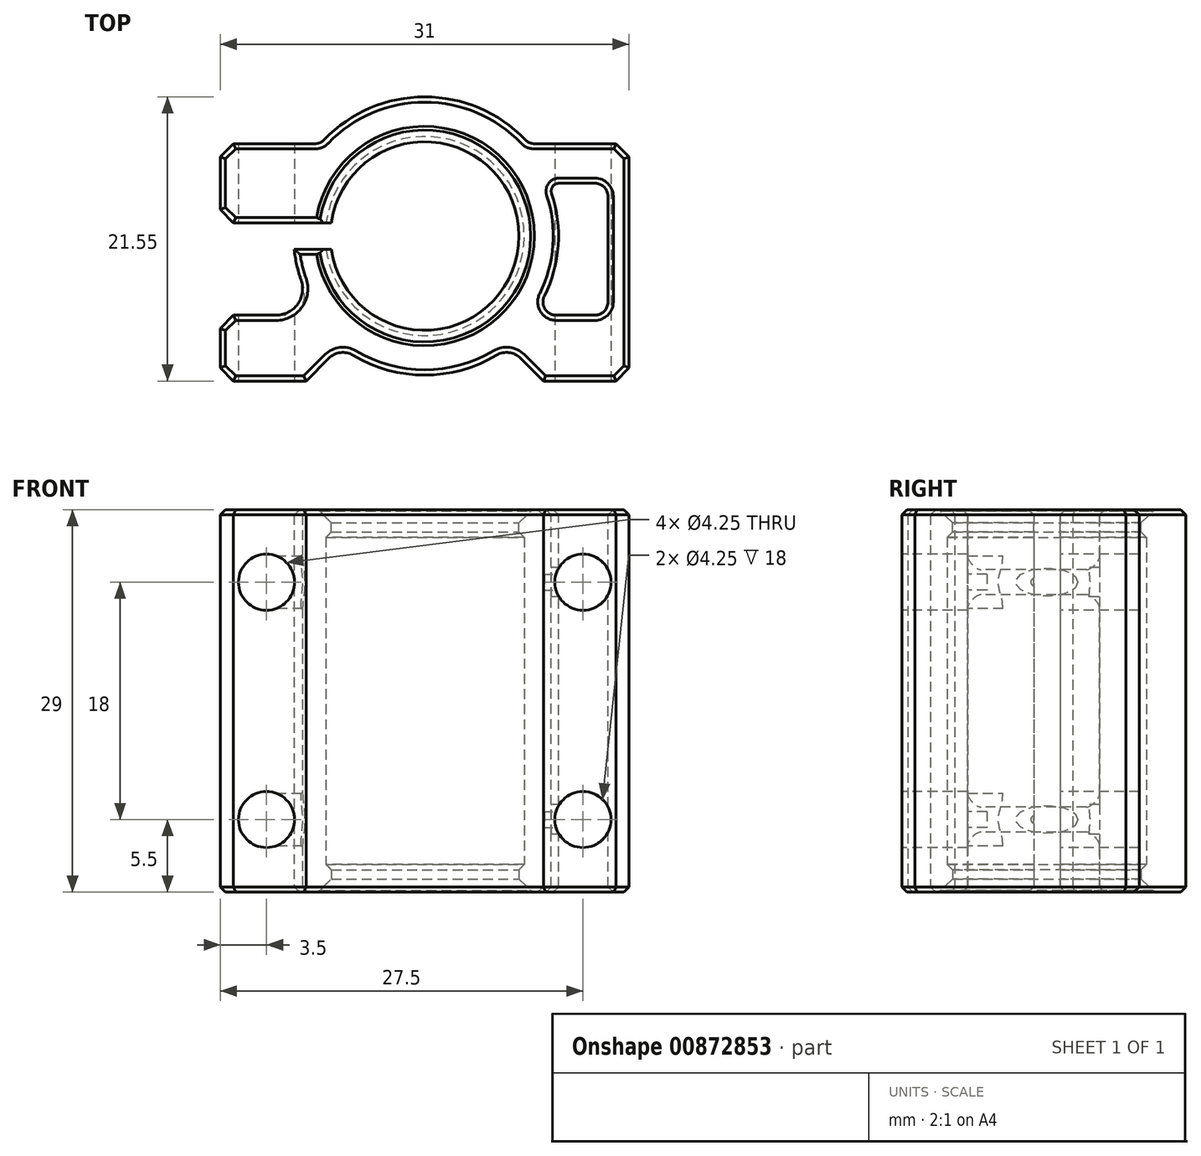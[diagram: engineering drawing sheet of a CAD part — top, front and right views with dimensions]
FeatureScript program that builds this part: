
annotation { "Feature Type Name" : "Feature", "Feature Type Description" : "" }
export const myFeature = defineFeature(function(context is Context, id is Id, definition is map)
    precondition{}
    {
        {
            var Q0;
            Q0=qCreatedBy(makeId("Top.planeOp"),FACE);
            var sketch = newSketch(context, id + "F0", { "sketchPlane" : qUnion([Q0])});
            skLineSegment(sketch, "E0", {"start": v(-15.5, 0) * mm, "end": v(-9, 0) * mm});
            skLineSegment(sketch, "E1", {"start": v(-9, 0) * mm, "end": v(-6.4, 2.6) * mm});
            skLineSegment(sketch, "E2", {"start": v(-15.5, 0) * mm, "end": v(-15.5, 5) * mm});
            skArc(sketch, "E3", {"start": v(0, 18.55) * mm, "mid": v(-4.97, 16.68) * mm, "end": v(-7.48, 12) * mm});
            skArc(sketch, "E4", {"start": v(0, 21.55) * mm, "mid": v(-4.33, 20.62) * mm, "end": v(-7.9, 18) * mm});
            skLineSegment(sketch, "E5", {"start": v(0, -24.75) * mm, "end": v(0, 26.18) * mm, "construction": true});
            skArc(sketch, "E6.MirrorCS", {"start": v(0, 18.55) * mm, "mid": v(7.55, 11) * mm, "end": v(0, 3.45) * mm});
            skArc(sketch, "E7.MirrorCS", {"start": v(0, 21.55) * mm, "mid": v(4.33, 20.62) * mm, "end": v(7.9, 18) * mm});
            skLineSegment(sketch, "E8.MirrorCS", {"start": v(15.5, 0) * mm, "end": v(15.5, 8) * mm});
            skLineSegment(sketch, "E9.MirrorCS", {"start": v(15.5, 0) * mm, "end": v(9, 0) * mm});
            skLineSegment(sketch, "E10.MirrorCS", {"start": v(9, 0) * mm, "end": v(6.4, 2.6) * mm});
            skLineSegment(sketch, "E11", {"start": v(-7.9, 18) * mm, "end": v(-15.5, 18) * mm});
            skLineSegment(sketch, "E12", {"start": v(-15.5, 18) * mm, "end": v(-15.5, 12) * mm});
            skLineSegment(sketch, "E13", {"start": v(-15.5, 12) * mm, "end": v(-10.5, 12) * mm});
            skLineSegment(sketch, "E14", {"start": v(-15.5, 12) * mm, "end": v(-15.5, 10) * mm, "construction": true});
            skLineSegment(sketch, "E15", {"start": v(-10.5, 12) * mm, "end": v(-7.48, 12) * mm});
            skLineSegment(sketch, "E16", {"start": v(-7.48, 10) * mm, "end": v(-9.9, 10) * mm});
            skArc(sketch, "E17.trimOffspring", {"start": v(-7.48, 10) * mm, "mid": v(-4.97, 5.32) * mm, "end": v(0, 3.45) * mm});
            skPoint(sketch, "E18.end.orphan", {"position": v(-8.84, 5.25) * mm});
            skLineSegment(sketch, "E19", {"start": v(7.9, 18) * mm, "end": v(15.5, 18) * mm});
            skLineSegment(sketch, "E20", {"start": v(15.5, 18) * mm, "end": v(15.5, 8) * mm});
            skPoint(sketch, "E21.orphan", {"position": v(8.84, 5.25) * mm});
            skArc(sketch, "E22", {"start": v(-6.4, 2.6) * mm, "mid": v(0, 0.45) * mm, "end": v(6.4, 2.6) * mm});
            skPoint(sketch, "E23.orphan", {"position": v(6.4, 2.6) * mm});
            skPoint(sketch, "E24.MirrorCS.end.orphan", {"position": v(0, 1) * mm});
            skLineSegment(sketch, "E25", {"start": v(-15.5, 5) * mm, "end": v(-7.94, 5) * mm});
            skArc(sketch, "E26.trimOffspring", {"start": v(-9.9, 10) * mm, "mid": v(-9.26, 7.37) * mm, "end": v(-7.94, 5) * mm});
            skPoint(sketch, "E27.orphan", {"position": v(-15.5, 10) * mm});
            skPoint(sketch, "E28.orphan", {"position": v(-15.5, 8) * mm});
            skSolve(sketch);
        }
        {
            var Q0;
            Q0=makeQuery(id+"F0.imprint","IMPRINT",FACE,{"disambiguationData":[TD([[makeQuery(id+"F0.imprint","IMPRINT",EDGE,{"derivedFrom":sQuery(id+"F0.wireOp",EDGE,"E0")}),1.0]])]});
            extrude(context, id + "F1", {"entities" : qUnion([Q0]), "depth" : 29 * mm, "offsetDistance" : 25 * mm});
        }
        {
            var Q0;
            Q0=makeQuery(id+"F1.opExtrude","SWEPT_EDGE",EDGE,{"disambiguationData":[OSD([sQuery(id+"F0.wireOp",EDGE,"E4"),sQuery(id+"F0.wireOp",EDGE,"E11")])]});
            var Q1;
            Q1=makeQuery(id+"F1.opExtrude","SWEPT_EDGE",EDGE,{"disambiguationData":[OSD([sQuery(id+"F0.wireOp",EDGE,"E7.MirrorCS"),sQuery(id+"F0.wireOp",EDGE,"E19")])]});
            fillet(context, id + "F2", {"entities" : qUnion([Q0, Q1]), "radius" : 1 * mm, "tangentPropagation" : true, "allowEdgeOverflow" : false});
        }
        {
            var Q0;
            Q0=makeQuery(id+"F1.opExtrude","SWEPT_EDGE",EDGE,{"disambiguationData":[OSD([sQuery(id+"F0.wireOp",EDGE,"44913da9-7672-4811-ad3e-e7159bf9c9510.MirrorCS"),sQuery(id+"F0.wireOp",EDGE,"E8.MirrorCS")])]});
            var Q1;
            Q1=makeQuery(id+"F1.opExtrude","SWEPT_EDGE",EDGE,{"disambiguationData":[OSD([sQuery(id+"F0.wireOp",EDGE,"E19"),sQuery(id+"F0.wireOp",EDGE,"E20")])]});
            var Q2;
            Q2=makeQuery(id+"F1.opExtrude","SWEPT_EDGE",EDGE,{"disambiguationData":[OSD([sQuery(id+"F0.wireOp",EDGE,"E0"),sQuery(id+"F0.wireOp",EDGE,"E2")])]});
            var Q3;
            Q3=makeQuery(id+"F1.opExtrude","SWEPT_EDGE",EDGE,{"disambiguationData":[OSD([sQuery(id+"F0.wireOp",EDGE,"E12"),sQuery(id+"F0.wireOp",EDGE,"E13")])]});
            var Q4;
            Q4=makeQuery(id+"F1.opExtrude","SWEPT_EDGE",EDGE,{"disambiguationData":[OSD([sQuery(id+"F0.wireOp",EDGE,"E11"),sQuery(id+"F0.wireOp",EDGE,"E12")])]});
            var Q5;
            Q5=makeQuery(id+"F1.opExtrude","SWEPT_EDGE",EDGE,{"disambiguationData":[OSD([sQuery(id+"F0.wireOp",EDGE,"E2"),sQuery(id+"F0.wireOp",EDGE,"E25")])]});
            chamfer(context, id + "F3", {"entities" : qUnion([Q0, Q1, Q2, Q3, Q4, Q5]), "width" : 1 * mm, "tangentPropagation" : true});
        }
        {
            var Q0;
            Q0=qCreatedBy(makeId("Front.planeOp"),FACE);
            var sketch = newSketch(context, id + "F4", { "sketchPlane" : qUnion([Q0])});
            skLineSegment(sketch, "E29.bottom", {"start": v(-12, 23.5) * mm, "end": v(12, 23.5) * mm, "construction": true});
            skLineSegment(sketch, "E29.top", {"start": v(-12, 5.5) * mm, "end": v(12, 5.5) * mm, "construction": true});
            skLineSegment(sketch, "E29.left", {"start": v(-12, 23.5) * mm, "end": v(-12, 5.5) * mm, "construction": true});
            skLineSegment(sketch, "E29.right", {"start": v(12, 23.5) * mm, "end": v(12, 5.5) * mm, "construction": true});
            skLineSegment(sketch, "E30", {"start": v(0, 0) * mm, "end": v(0, 29) * mm, "construction": true});
            skLineSegment(sketch, "E31", {"start": v(0, 14.5) * mm, "end": v(18.51, 14.5) * mm, "construction": true});
            skCircle(sketch, "E32", {"center": v(12, 23.5) * mm, "radius": 2.12 * mm});
            skCircle(sketch, "E33", {"center": v(-12, 23.5) * mm, "radius": 2.12 * mm});
            skCircle(sketch, "E34", {"center": v(12, 5.5) * mm, "radius": 2.12 * mm});
            skCircle(sketch, "E35", {"center": v(-12, 5.5) * mm, "radius": 2.12 * mm});
            skSolve(sketch);
        }
        {
            var Q0;
            Q0 = qSketchRegion(id + "F4", true);
            extrude(context, id + "F5", {"entities" : qUnion([Q0]), "operationType" : NewBodyOperationType.REMOVE, "endBound" : BoundingType.THROUGH_ALL, "oppositeDirection" : true, "depth" : 25 * mm, "offsetDistance" : 25 * mm});
        }
        {
            var Q0;
            Q0=makeQuery(id+"F1.opExtrude","CAP_FACE",FACE,{"disambiguationData":[OSD([sQuery(id+"F0.wireOp",EDGE,"E0"),sQuery(id+"F0.wireOp",EDGE,"E1"),sQuery(id+"F0.wireOp",EDGE,"0b3265f1-5941-46db-a906-9e62640ea9ff"),sQuery(id+"F0.wireOp",EDGE,"E2"),sQuery(id+"F0.wireOp",EDGE,"E3"),sQuery(id+"F0.wireOp",EDGE,"E4"),sQuery(id+"F0.wireOp",EDGE,"E6.MirrorCS"),sQuery(id+"F0.wireOp",EDGE,"E7.MirrorCS"),sQuery(id+"F0.wireOp",EDGE,"44913da9-7672-4811-ad3e-e7159bf9c9510.MirrorCS"),sQuery(id+"F0.wireOp",EDGE,"E8.MirrorCS"),sQuery(id+"F0.wireOp",EDGE,"E9.MirrorCS"),sQuery(id+"F0.wireOp",EDGE,"E24.MirrorCS"),sQuery(id+"F0.wireOp",EDGE,"E10.MirrorCS"),sQuery(id+"F0.wireOp",EDGE,"E11"),sQuery(id+"F0.wireOp",EDGE,"E12"),sQuery(id+"F0.wireOp",EDGE,"E13"),sQuery(id+"F0.wireOp",EDGE,"E15"),sQuery(id+"F0.wireOp",EDGE,"E16"),sQuery(id+"F0.wireOp",EDGE,"2c5662f4-6ae5-41bf-b86e-1c826bd00076"),sQuery(id+"F0.wireOp",EDGE,"E17.trimOffspring")])],"isStart":false});
            var sketch = newSketch(context, id + "F6", { "sketchPlane" : qUnion([Q0])});
            skArc(sketch, "E36.0", {"start": v(-7.48, 10) * mm, "mid": v(7.55, 11) * mm, "end": v(-7.48, 12) * mm});
            skArc(sketch, "E37", {"start": v(-7.08, 10) * mm, "mid": v(7.15, 11) * mm, "end": v(-7.08, 12) * mm});
            skLineSegment(sketch, "E38", {"start": v(-7.48, 12) * mm, "end": v(-7.08, 12) * mm});
            skLineSegment(sketch, "E39", {"start": v(-7.48, 10) * mm, "end": v(-7.08, 10) * mm});
            skSolve(sketch);
        }
        {
            var Q0;
            Q0=makeQuery(id+"F6.imprint","IMPRINT",FACE,{"disambiguationData":[TD([[makeQuery(id+"F6.imprint","IMPRINT",EDGE,{"derivedFrom":sQuery(id+"F6.wireOp",EDGE,"E36.0")}),1.0]])]});
            extrude(context, id + "F7", {"entities" : qUnion([Q0]), "oppositeDirection" : true, "depth" : 2.1 * mm, "offsetDistance" : 25 * mm});
        }
        {
            var Q0;
            Q0=makeQuery(id+"F1.opExtrude","CAP_FACE",FACE,{"disambiguationData":[OSD([sQuery(id+"F0.wireOp",EDGE,"E0"),sQuery(id+"F0.wireOp",EDGE,"E1"),sQuery(id+"F0.wireOp",EDGE,"0b3265f1-5941-46db-a906-9e62640ea9ff"),sQuery(id+"F0.wireOp",EDGE,"E2"),sQuery(id+"F0.wireOp",EDGE,"E3"),sQuery(id+"F0.wireOp",EDGE,"E4"),sQuery(id+"F0.wireOp",EDGE,"E6.MirrorCS"),sQuery(id+"F0.wireOp",EDGE,"E7.MirrorCS"),sQuery(id+"F0.wireOp",EDGE,"44913da9-7672-4811-ad3e-e7159bf9c9510.MirrorCS"),sQuery(id+"F0.wireOp",EDGE,"E8.MirrorCS"),sQuery(id+"F0.wireOp",EDGE,"E9.MirrorCS"),sQuery(id+"F0.wireOp",EDGE,"E24.MirrorCS"),sQuery(id+"F0.wireOp",EDGE,"E10.MirrorCS"),sQuery(id+"F0.wireOp",EDGE,"E11"),sQuery(id+"F0.wireOp",EDGE,"E12"),sQuery(id+"F0.wireOp",EDGE,"E13"),sQuery(id+"F0.wireOp",EDGE,"E15"),sQuery(id+"F0.wireOp",EDGE,"E16"),sQuery(id+"F0.wireOp",EDGE,"2c5662f4-6ae5-41bf-b86e-1c826bd00076"),sQuery(id+"F0.wireOp",EDGE,"E17.trimOffspring")])],"isStart":true});
            var sketch = newSketch(context, id + "F8", { "sketchPlane" : qUnion([Q0])});
            skArc(sketch, "E40.0", {"start": v(-7.48, -10) * mm, "mid": v(7.55, -11) * mm, "end": v(-7.48, -12) * mm});
            skArc(sketch, "E41.0", {"start": v(-7.08, -10) * mm, "mid": v(7.15, -11) * mm, "end": v(-7.08, -12) * mm});
            skLineSegment(sketch, "E42.0", {"start": v(-7.48, -10) * mm, "end": v(-7.08, -10) * mm});
            skLineSegment(sketch, "E43.0", {"start": v(-7.48, -12) * mm, "end": v(-7.08, -12) * mm});
            skSolve(sketch);
        }
        {
            var Q0;
            Q0 = qSketchRegion(id + "F8", true);
            extrude(context, id + "F9", {"entities" : qUnion([Q0]), "operationType" : NewBodyOperationType.ADD, "oppositeDirection" : true, "depth" : 2.1 * mm, "offsetDistance" : 25 * mm});
        }
        {
            var Q0;
            Q0=makeQuery(id+"F1.opExtrude","SWEPT_BODY",BODY,{"disambiguationData":[OSD([sQuery(id+"F0.wireOp",EDGE,"E0"),sQuery(id+"F0.wireOp",EDGE,"E1"),sQuery(id+"F0.wireOp",EDGE,"0b3265f1-5941-46db-a906-9e62640ea9ff"),sQuery(id+"F0.wireOp",EDGE,"E2"),sQuery(id+"F0.wireOp",EDGE,"E3"),sQuery(id+"F0.wireOp",EDGE,"E4"),sQuery(id+"F0.wireOp",EDGE,"E6.MirrorCS"),sQuery(id+"F0.wireOp",EDGE,"E7.MirrorCS"),sQuery(id+"F0.wireOp",EDGE,"44913da9-7672-4811-ad3e-e7159bf9c9510.MirrorCS"),sQuery(id+"F0.wireOp",EDGE,"E8.MirrorCS"),sQuery(id+"F0.wireOp",EDGE,"E9.MirrorCS"),sQuery(id+"F0.wireOp",EDGE,"E24.MirrorCS"),sQuery(id+"F0.wireOp",EDGE,"E10.MirrorCS"),sQuery(id+"F0.wireOp",EDGE,"E11"),sQuery(id+"F0.wireOp",EDGE,"E12"),sQuery(id+"F0.wireOp",EDGE,"E13"),sQuery(id+"F0.wireOp",EDGE,"E15"),sQuery(id+"F0.wireOp",EDGE,"E16"),sQuery(id+"F0.wireOp",EDGE,"2c5662f4-6ae5-41bf-b86e-1c826bd00076"),sQuery(id+"F0.wireOp",EDGE,"E17.trimOffspring")])]});
            var Q1;
            Q1=makeQuery(id+"F7.opExtrude","SWEPT_BODY",BODY,{"disambiguationData":[OSD([sQuery(id+"F6.wireOp",EDGE,"E36.0"),sQuery(id+"F6.wireOp",EDGE,"E37"),sQuery(id+"F6.wireOp",EDGE,"E38"),sQuery(id+"F6.wireOp",EDGE,"E39")])]});
            booleanBodies(context, id + "F10", {"operationType" : BooleanOperationType.UNION, "tools" : qUnion([Q0, Q1])});
        }
        {
            var Q0;
            Q0=makeQuery(id+"F7.opExtrude","CAP_EDGE",EDGE,{"disambiguationData":[OSD([sQuery(id+"F6.wireOp",EDGE,"E37")])],"isStart":false});
            var Q1;
            Q1=makeQuery(id+"F9.opExtrude","CAP_EDGE",EDGE,{"disambiguationData":[OSD([sQuery(id+"F8.wireOp",EDGE,"E41.0")])],"isStart":false});
            chamfer(context, id + "F11", {"entities" : qUnion([Q0, Q1]), "width" : 0.4 * mm, "tangentPropagation" : true});
        }
        {
            var Q0;
            Q0=makeQuery(id+"F10.opBoolean","MERGE",FACE,{"derivedFrom":[makeQuery(id+"F1.opExtrude","CAP_FACE",FACE,{"disambiguationData":[OSD([sQuery(id+"F0.wireOp",EDGE,"E0"),sQuery(id+"F0.wireOp",EDGE,"E1"),sQuery(id+"F0.wireOp",EDGE,"0b3265f1-5941-46db-a906-9e62640ea9ff"),sQuery(id+"F0.wireOp",EDGE,"E2"),sQuery(id+"F0.wireOp",EDGE,"E3"),sQuery(id+"F0.wireOp",EDGE,"E4"),sQuery(id+"F0.wireOp",EDGE,"E6.MirrorCS"),sQuery(id+"F0.wireOp",EDGE,"E7.MirrorCS"),sQuery(id+"F0.wireOp",EDGE,"E8.MirrorCS"),sQuery(id+"F0.wireOp",EDGE,"E9.MirrorCS"),sQuery(id+"F0.wireOp",EDGE,"E24.MirrorCS"),sQuery(id+"F0.wireOp",EDGE,"E10.MirrorCS"),sQuery(id+"F0.wireOp",EDGE,"E11"),sQuery(id+"F0.wireOp",EDGE,"E12"),sQuery(id+"F0.wireOp",EDGE,"E13"),sQuery(id+"F0.wireOp",EDGE,"E15"),sQuery(id+"F0.wireOp",EDGE,"E16"),sQuery(id+"F0.wireOp",EDGE,"2c5662f4-6ae5-41bf-b86e-1c826bd00076"),sQuery(id+"F0.wireOp",EDGE,"E17.trimOffspring"),sQuery(id+"F0.wireOp",EDGE,"E19"),sQuery(id+"F0.wireOp",EDGE,"E20")])],"isStart":false}),makeQuery(id+"F7.opExtrude","CAP_FACE",FACE,{"disambiguationData":[OSD([sQuery(id+"F6.wireOp",EDGE,"E36.0"),sQuery(id+"F6.wireOp",EDGE,"E37"),sQuery(id+"F6.wireOp",EDGE,"E38"),sQuery(id+"F6.wireOp",EDGE,"E39")])],"isStart":true})]});
            var sketch = newSketch(context, id + "F12", { "sketchPlane" : qUnion([Q0])});
            skArc(sketch, "E44.0", {"start": v(8.19, 5) * mm, "mid": v(10.08, 9.85) * mm, "end": v(9.33, 15) * mm});
            skLineSegment(sketch, "E45.0", {"start": v(13.9, 5) * mm, "end": v(13.9, 15) * mm});
            skLineSegment(sketch, "E46", {"start": v(9.33, 15) * mm, "end": v(13.9, 15) * mm});
            skLineSegment(sketch, "E47", {"start": v(8.19, 5) * mm, "end": v(13.9, 5) * mm});
            skSolve(sketch);
        }
        {
            var Q0;
            Q0=makeQuery(id+"F12.imprint","IMPRINT",FACE,{"disambiguationData":[TD([[makeQuery(id+"F12.imprint","IMPRINT",EDGE,{"derivedFrom":sQuery(id+"F12.wireOp",EDGE,"E44.0")}),-1.0]])]});
            extrude(context, id + "F13", {"entities" : qUnion([Q0]), "operationType" : NewBodyOperationType.REMOVE, "endBound" : BoundingType.THROUGH_ALL, "oppositeDirection" : true, "depth" : 25 * mm, "offsetDistance" : 25 * mm});
        }
        {
            var Q0;
            Q0=makeQuery(id+"F13.boolean.opBoolean","COPY",EDGE,{"derivedFrom":makeQuery(id+"F13.opExtrude","SWEPT_EDGE",EDGE,{"disambiguationData":[OSD([sQuery(id+"F12.wireOp",EDGE,"E44.0"),sQuery(id+"F12.wireOp",EDGE,"E47")])]})});
            fillet(context, id + "F14", {"entities" : qUnion([Q0]), "radius" : 1 * mm, "tangentPropagation" : true, "allowEdgeOverflow" : false});
        }
        {
            var Q0;
            Q0=makeQuery(id+"F13.boolean.opBoolean","COPY",EDGE,{"derivedFrom":makeQuery(id+"F13.opExtrude","SWEPT_EDGE",EDGE,{"disambiguationData":[OSD([sQuery(id+"F12.wireOp",EDGE,"E44.0"),sQuery(id+"F12.wireOp",EDGE,"E46")])]})});
            fillet(context, id + "F15", {"entities" : qUnion([Q0]), "radius" : 0.6 * mm, "tangentPropagation" : true, "allowEdgeOverflow" : false});
        }
        {
            var Q0;
            Q0=makeQuery(id+"F1.opExtrude","SWEPT_EDGE",EDGE,{"disambiguationData":[OSD([sQuery(id+"F0.wireOp",EDGE,"E1"),sQuery(id+"F0.wireOp",EDGE,"E22")])]});
            var Q1;
            Q1=makeQuery(id+"F1.opExtrude","SWEPT_EDGE",EDGE,{"disambiguationData":[OSD([sQuery(id+"F0.wireOp",EDGE,"E10.MirrorCS"),sQuery(id+"F0.wireOp",EDGE,"E22")])]});
            fillet(context, id + "F16", {"entities" : qUnion([Q0, Q1]), "radius" : 1.5 * mm, "tangentPropagation" : true, "allowEdgeOverflow" : false});
        }
        {
            var Q0;
            Q0=makeQuery(id+"F13.boolean.opBoolean","COPY",EDGE,{"derivedFrom":makeQuery(id+"F13.opExtrude","SWEPT_EDGE",EDGE,{"disambiguationData":[OSD([sQuery(id+"F12.wireOp",EDGE,"E45.0"),sQuery(id+"F12.wireOp",EDGE,"E47")])]})});
            var Q1;
            Q1=makeQuery(id+"F13.boolean.opBoolean","COPY",EDGE,{"derivedFrom":makeQuery(id+"F13.opExtrude","SWEPT_EDGE",EDGE,{"disambiguationData":[OSD([sQuery(id+"F12.wireOp",EDGE,"E45.0"),sQuery(id+"F12.wireOp",EDGE,"E46")])]})});
            fillet(context, id + "F17", {"entities" : qUnion([Q0, Q1]), "radius" : 1 * mm, "tangentPropagation" : true, "allowEdgeOverflow" : false});
        }
        {
            var Q0;
            Q0=makeQuery(id+"F1.opExtrude","SWEPT_EDGE",EDGE,{"disambiguationData":[OSD([sQuery(id+"F0.wireOp",EDGE,"E25"),sQuery(id+"F0.wireOp",EDGE,"E26.trimOffspring")])]});
            fillet(context, id + "F18", {"entities" : qUnion([Q0]), "radius" : 2 * mm, "tangentPropagation" : true, "allowEdgeOverflow" : false});
        }
        {
            var Q0;
            Q0=makeQuery(id+"F9.opExtrude","CAP_EDGE",EDGE,{"disambiguationData":[OSD([sQuery(id+"F8.wireOp",EDGE,"E41.0")])],"isStart":true});
            var Q1;
            Q1=makeQuery(id+"F7.opExtrude","CAP_EDGE",EDGE,{"disambiguationData":[OSD([sQuery(id+"F6.wireOp",EDGE,"E37")])],"isStart":true});
            chamfer(context, id + "F19", {"entities" : qUnion([Q0, Q1]), "width" : 1 * mm, "tangentPropagation" : true});
        }
        {
            var Q0;
            Q0=makeQuery(id+"F10.opBoolean","MERGE",FACE,{"derivedFrom":[makeQuery(id+"F1.opExtrude","CAP_FACE",FACE,{"disambiguationData":[OSD([sQuery(id+"F0.wireOp",EDGE,"E0"),sQuery(id+"F0.wireOp",EDGE,"E1"),sQuery(id+"F0.wireOp",EDGE,"0b3265f1-5941-46db-a906-9e62640ea9ff"),sQuery(id+"F0.wireOp",EDGE,"E2"),sQuery(id+"F0.wireOp",EDGE,"E3"),sQuery(id+"F0.wireOp",EDGE,"E4"),sQuery(id+"F0.wireOp",EDGE,"E6.MirrorCS"),sQuery(id+"F0.wireOp",EDGE,"E7.MirrorCS"),sQuery(id+"F0.wireOp",EDGE,"E8.MirrorCS"),sQuery(id+"F0.wireOp",EDGE,"E9.MirrorCS"),sQuery(id+"F0.wireOp",EDGE,"E24.MirrorCS"),sQuery(id+"F0.wireOp",EDGE,"E10.MirrorCS"),sQuery(id+"F0.wireOp",EDGE,"E11"),sQuery(id+"F0.wireOp",EDGE,"E12"),sQuery(id+"F0.wireOp",EDGE,"E13"),sQuery(id+"F0.wireOp",EDGE,"E15"),sQuery(id+"F0.wireOp",EDGE,"E16"),sQuery(id+"F0.wireOp",EDGE,"2c5662f4-6ae5-41bf-b86e-1c826bd00076"),sQuery(id+"F0.wireOp",EDGE,"E17.trimOffspring"),sQuery(id+"F0.wireOp",EDGE,"E19"),sQuery(id+"F0.wireOp",EDGE,"E20")])],"isStart":false}),makeQuery(id+"F7.opExtrude","CAP_FACE",FACE,{"disambiguationData":[OSD([sQuery(id+"F6.wireOp",EDGE,"E36.0"),sQuery(id+"F6.wireOp",EDGE,"E37"),sQuery(id+"F6.wireOp",EDGE,"E38"),sQuery(id+"F6.wireOp",EDGE,"E39")])],"isStart":true})]});
            var Q1;
            Q1=makeQuery(id+"F1.opExtrude","CAP_EDGE",EDGE,{"disambiguationData":[OSD([sQuery(id+"F0.wireOp",EDGE,"E11")])],"isStart":false});
            var Q2;
            Q2=makeQuery(id+"F9.boolean.opBoolean","MERGE",FACE,{"derivedFrom":[makeQuery(id+"F1.opExtrude","CAP_FACE",FACE,{"disambiguationData":[OSD([sQuery(id+"F0.wireOp",EDGE,"E0"),sQuery(id+"F0.wireOp",EDGE,"E1"),sQuery(id+"F0.wireOp",EDGE,"0b3265f1-5941-46db-a906-9e62640ea9ff"),sQuery(id+"F0.wireOp",EDGE,"E2"),sQuery(id+"F0.wireOp",EDGE,"E3"),sQuery(id+"F0.wireOp",EDGE,"E4"),sQuery(id+"F0.wireOp",EDGE,"E6.MirrorCS"),sQuery(id+"F0.wireOp",EDGE,"E7.MirrorCS"),sQuery(id+"F0.wireOp",EDGE,"E8.MirrorCS"),sQuery(id+"F0.wireOp",EDGE,"E9.MirrorCS"),sQuery(id+"F0.wireOp",EDGE,"E24.MirrorCS"),sQuery(id+"F0.wireOp",EDGE,"E10.MirrorCS"),sQuery(id+"F0.wireOp",EDGE,"E11"),sQuery(id+"F0.wireOp",EDGE,"E12"),sQuery(id+"F0.wireOp",EDGE,"E13"),sQuery(id+"F0.wireOp",EDGE,"E15"),sQuery(id+"F0.wireOp",EDGE,"E16"),sQuery(id+"F0.wireOp",EDGE,"2c5662f4-6ae5-41bf-b86e-1c826bd00076"),sQuery(id+"F0.wireOp",EDGE,"E17.trimOffspring"),sQuery(id+"F0.wireOp",EDGE,"E19"),sQuery(id+"F0.wireOp",EDGE,"E20")])],"isStart":true}),makeQuery(id+"F9.opExtrude","CAP_FACE",FACE,{"disambiguationData":[OSD([sQuery(id+"F8.wireOp",EDGE,"E40.0"),sQuery(id+"F8.wireOp",EDGE,"E41.0"),sQuery(id+"F8.wireOp",EDGE,"E42.0"),sQuery(id+"F8.wireOp",EDGE,"E43.0")])],"isStart":true})]});
            chamfer(context, id + "F20", {"entities" : qUnion([Q0, Q1, Q2]), "width" : 0.4 * mm, "tangentPropagation" : true});
        }
    });
